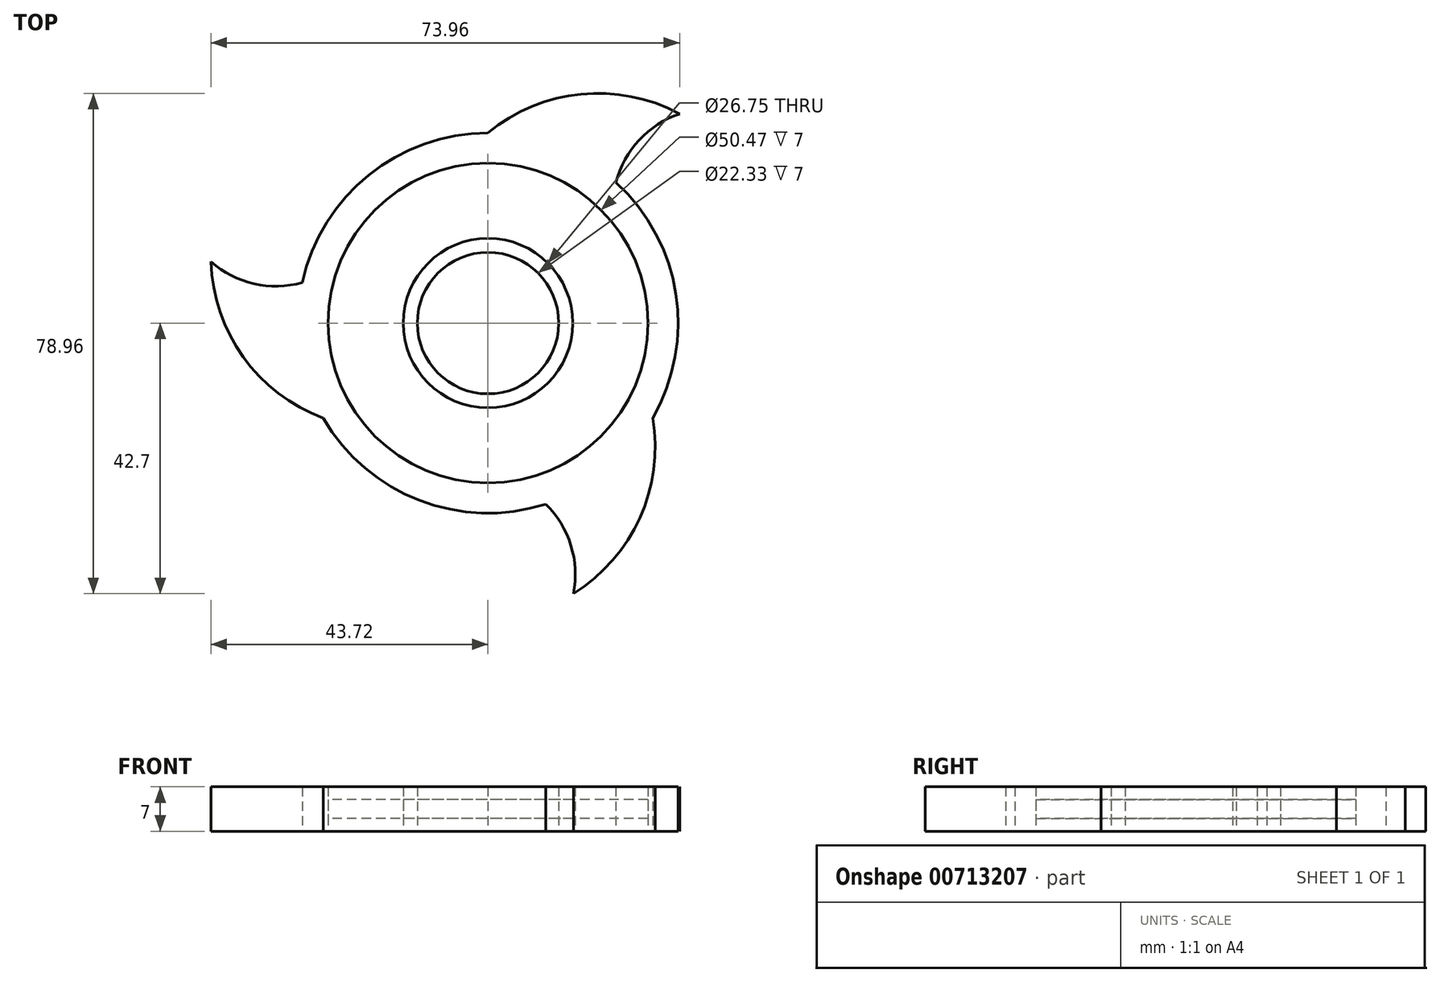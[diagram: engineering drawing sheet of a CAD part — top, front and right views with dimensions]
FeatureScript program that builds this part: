
annotation { "Feature Type Name" : "Feature", "Feature Type Description" : "" }
export const myFeature = defineFeature(function(context is Context, id is Id, definition is map)
    precondition{}
    {
        {
            var Q0;
            Q0=qCreatedBy(makeId("Top.planeOp"),FACE);
            var sketch = newSketch(context, id + "F0", { "sketchPlane" : qUnion([Q0])});
            skCircle(sketch, "E0", {"center": v(0, 0) * mm, "radius": 30 * mm});
            skCircle(sketch, "E1", {"center": v(0, 0) * mm, "radius": 11.16 * mm});
            skArc(sketch, "E2", {"start": v(30.24, 33.02) * mm, "mid": v(14.66, 36.13) * mm, "end": v(0, 30) * mm});
            skArc(sketch, "E3", {"start": v(30.24, 33.02) * mm, "mid": v(23.85, 28.88) * mm, "end": v(20.18, 22.2) * mm});
            skArc(sketch, "E4.1.0", {"start": v(-43.72, 9.68) * mm, "mid": v(-38.62, -5.37) * mm, "end": v(-25.98, -15) * mm});
            skArc(sketch, "E4.1.1", {"start": v(-43.72, 9.68) * mm, "mid": v(-36.93, 6.22) * mm, "end": v(-29.31, 6.38) * mm});
            skArc(sketch, "E4.2.0", {"start": v(13.48, -42.7) * mm, "mid": v(23.96, -30.76) * mm, "end": v(25.98, -15) * mm});
            skArc(sketch, "E4.2.1", {"start": v(13.48, -42.7) * mm, "mid": v(13.08, -35.1) * mm, "end": v(9.14, -28.58) * mm});
            skCircle(sketch, "E5", {"center": v(0, 0) * mm, "radius": 13.37 * mm});
            skCircle(sketch, "E6", {"center": v(0, 0) * mm, "radius": 25.23 * mm});
            skSolve(sketch);
        }
        {
            var Q0;
            Q0=makeQuery(id+"F0.imprint","IMPRINT",FACE,{"disambiguationData":[TD([[makeQuery(id+"F0.imprint","IMPRINT",EDGE,{"derivedFrom":sQuery(id+"F0.wireOp",EDGE,"E1")}),-1.0]])]});
            var Q1;
            Q1=makeQuery(id+"F0.imprint","IMPRINT",FACE,{"disambiguationData":[TD([[makeQuery(id+"F0.imprint","IMPRINT",EDGE,{"derivedFrom":sQuery(id+"F0.wireOp",EDGE,"E6")}),-1.0]])]});
            var Q2;
            {var subQ0=sQuery(id+"F0.wireOp",EDGE,"E2");Q2=makeQuery(id+"F0.imprint","IMPRINT",FACE,{"disambiguationData":[TD([[makeQuery(id+"F0.imprint","IMPRINT",EDGE,{"derivedFrom":subQ0}),1.0]])]});}
            var Q3;
            {var subQ0=sQuery(id+"F0.wireOp",EDGE,"E4.1.0");Q3=makeQuery(id+"F0.imprint","IMPRINT",FACE,{"disambiguationData":[TD([[makeQuery(id+"F0.imprint","IMPRINT",EDGE,{"derivedFrom":subQ0}),1.0]])]});}
            var Q4;
            {var subQ0=sQuery(id+"F0.wireOp",EDGE,"E4.2.0");Q4=makeQuery(id+"F0.imprint","IMPRINT",FACE,{"disambiguationData":[TD([[makeQuery(id+"F0.imprint","IMPRINT",EDGE,{"derivedFrom":subQ0}),1.0]])]});}
            extrude(context, id + "F1", {"entities" : qUnion([Q0, Q1, Q2, Q3, Q4]), "depth" : 7 * mm, "offsetDistance" : 25 * mm});
        }
        {
            var Q0;
            Q0=makeQuery(id+"F0.imprint","IMPRINT",FACE,{"disambiguationData":[TD([[makeQuery(id+"F0.imprint","IMPRINT",EDGE,{"derivedFrom":sQuery(id+"F0.wireOp",EDGE,"E5")}),-1.0]])]});
            extrude(context, id + "F2", {"entities" : qUnion([Q0]), "depth" : 5 * mm, "offsetDistance" : 25 * mm});
        }
        {
            var Q0;
            Q0=makeQuery(id+"F0.imprint","IMPRINT",FACE,{"disambiguationData":[TD([[makeQuery(id+"F0.imprint","IMPRINT",EDGE,{"derivedFrom":sQuery(id+"F0.wireOp",EDGE,"E5")}),-1.0]])]});
            extrude(context, id + "F3", {"entities" : qUnion([Q0]), "operationType" : NewBodyOperationType.REMOVE, "depth" : 2 * mm, "offsetDistance" : 25 * mm});
        }
    });
